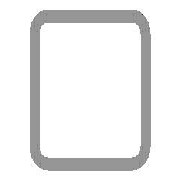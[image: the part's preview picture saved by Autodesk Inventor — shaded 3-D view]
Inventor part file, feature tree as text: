
AUTODESK INVENTOR PART (.ipt)
format: ipt  version: 2025.3 (Build 293356030, 356C)  size: 146,944 bytes
history: native  units: mm (DEFAULTED — no unit token found)
features: other x4, sketch x1, plane x1
ambient origin geometry x8: Origin, YZ Plane, XZ Plane, XY Plane, X Axis, Y Axis, Z Axis, Center Point
bodies: Solid1 (feature_tree), Body (feature_tree)
feature tree (6):
  parser-record x1  (decoder bookkeeping rows leaked as tree rows — omitted from the tree; the rows remain in map.json)
  other  "Driven Length"
  other  "Start Plane"
  other  "End Plane"
  sketch  "Sketch3"  dims[d3=560.0mm d4=0.0mm d7=4.0mm d9=40.0mm d11=40.0mm d12=2.0mm d13=-0.0mm d14=560.0mm d15=20.0mm d16=20.0mm d17=90.0deg d18=560.0mm]
  plane  "Work Plane3"
